# Revit family: Lighting_Fixtures_Hill-Rom_TruLight550-Surgical-Lights-TL510
name_source: partatom
category: Lighting Fixtures
revit_build: Autodesk Revit Architecture 2015 (Build: 20140606_1530(x64)
units: mm (PartAtom-declared; Revit-internal decimal feet)

## types (4) — shared parameters
ALC Plus = Standard
Apparent Load = 0 VA
Average service life of the LEDs = >40000
BIMobject category = All
BIMobject category code = medical-all
BIMobject main category = Medical
BIMobject main category code = medical
Brand url = https://construction.hill-rom.com
Camera Preparation = Standard
Color Filter = 16777215
Color Rendering Index (Ra) = max 96
Color temperature adjustable at the control panel = Option
Default Elevation = 4' - 0"
Description = TruLight™ 5500 Surgical Light's design makes the light easy to operate and offers flexibility and multiple future options for your hospital
Design country = United States
Dimming Lamp Color Temperature Shift = <None>
Edition number = 1
Frequency Range = 50-60 Hz
Full Load Current = 20 A
Illumination level Ec at 1m = 160000 lx
Installation instructions = https://construction.hill-rom.com
Light Source Symbol Size = 2' - 0"
Manufacturer = Hill-Rom
Manufacturer country = United States
Manufacturer name = Hill-Rom
Masterformat 2014 Code = 26 55 70
Masterformat 2014 Description = Healthcare Lighting
Material_display = Glass-Hill-Rom-Display
Material_handles = Plastic-Hill-Rom-Blue
Material_main = Plastic-Hill-Rom-White
Max Amperage = 0 A
Model = TruLight® 5500 Surgical Lights (TL510, Single Head)
Nominal height = 0' - 0"
Nominal width = 0' - 0"
OmniClass Code = 23-35 47 11 21
OmniClass Description = Specialized Lighting Fixtures
Power Connector Description = Power Connector Description
Power Consumption (max) = 60 W
Power Factor = 1
Product Guid = b4af10b6-62be-4e02-9973-ca820b09fc64
Product SKU = Trumpf-TruLight5500
Product data url = https://bimobject.com
Product family = Surgical Lights
Product group = TruLight 5500
Product url = https://www.trumpfmedical.com
QR code = http://bimobject.com
Relative humidity = 30% to 75%
SLC = -
Technical description = https://construction.hill-rom.com
UNSPSC Code = 39101602
URL = https://www.hill-rom.com
Uniclass 1.4 Code = L747331
Uniclass 1.4 Description = Medical/hospital lighting
Voltage = 120 V
Youtube clip = https://www.youtube.com

## per-type parameters (varying)
| type | Color Temperature | Frequency | Pattern distance variation | Pattern size at 1m |
| TruLight 5500 Surgical Lights - TL510 Single Head -5000K | 5000 K | 50 Hz | 16/23 / 6.3"/9.1" | 16-30 / 6.3"-11.8" |
| TruLight 5500 Surgical Lights - TL510 Single Head -4500K | 4500 K | 0 Hz | 16/23 / 6.3"/9.1" | 16-30 / 6.3"-11.8" |
| TruLight 5500 Surgical Lights - TL510 Single Head -4000K | 4000 K | 0 Hz | 16/23 / 6.3"/9.1" | 16-30 / 6.3"-11.8" |
| TruLight 5500 Surgical Lights - TL510 Single Head -3500K | 3500 K | 0 Hz | 16/23 cm / 6.3"/9.1" | 16-30 cm / 6.3"-11.8" |

## geometry (parser evidence)
native form markers: Blend x6, Sweep x3
no freeform markers — native parametric forms only
